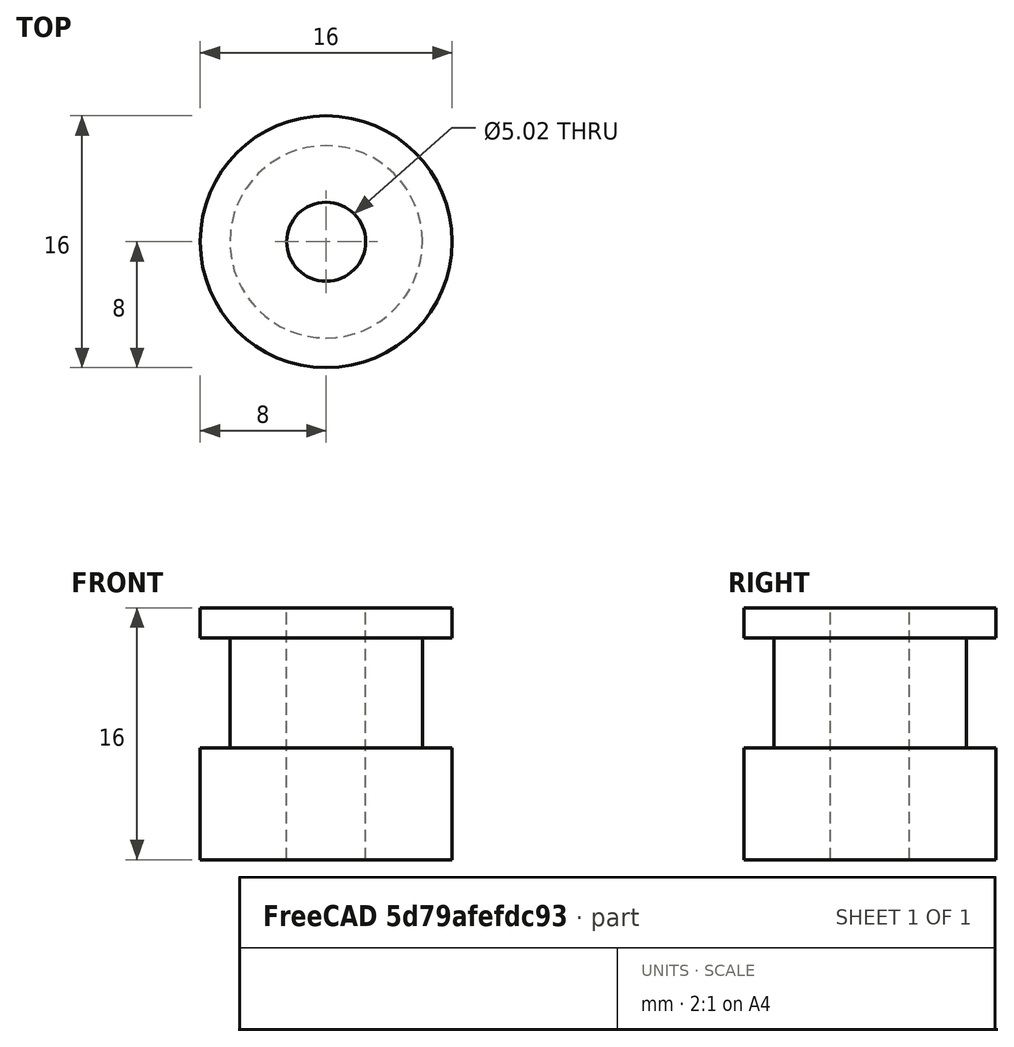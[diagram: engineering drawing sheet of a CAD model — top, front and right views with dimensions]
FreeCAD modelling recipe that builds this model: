
FCSTD DOCUMENT  (FreeCAD 0.20R29177 +426 (Git))
Label: TimingPulleyGT2
License: All rights reserved
LicenseURL: http://en.wikipedia.org/wiki/All_rights_reserved
objects: App::DocumentObjectGroup×3, PartDesign::CoordinateSystem×1, App::FeaturePython×1, Sketcher::SketchObject×1, PartDesign::Revolution×1, PartDesign::Body×1, App::Part×1
note: 5 computed .brp shape members not serialized (recipe doc carries the construction recipe); baked Part::Feature solids carry a one-line shape summary decoded from their .brp

FEATURE [App::DocumentObjectGroup] Parts
FEATURE [PartDesign::CoordinateSystem] LCS_Origin
  AttacherType = Attacher::AttachEngine3D
  MapMode = 2
  Support = -> [X_Axis]
FEATURE [App::FeaturePython] Variables  # WARN: FeaturePython — macro-defined, semantics opaque (R4)
  Type = App::PropertyContainer
FEATURE [App::DocumentObjectGroup] Constraints
FEATURE [App::DocumentObjectGroup] Configurations
FEATURE [Sketcher::SketchObject] Sketch
  FullyConstrained = true
  MapMode = 5
  Placement = pos=(0,0,0) rot=(1,0,0;1.5708rad)
  Support = -> [XZ_Plane001]
  sketch-geometry (8):
    g0: LineSegment StartX=2.51 StartY=0 StartZ=0 EndX=2.51 EndY=16 EndZ=0
    g1: LineSegment StartX=2.51 StartY=16 StartZ=0 EndX=8 EndY=16 EndZ=0
    g2: LineSegment StartX=8 StartY=16 StartZ=0 EndX=8 EndY=14.1 EndZ=0
    g3: LineSegment StartX=8 StartY=14.1 StartZ=0 EndX=6.11 EndY=14.1 EndZ=0
    g4: LineSegment StartX=6.11 StartY=14.1 StartZ=0 EndX=6.11 EndY=7.1 EndZ=0
    g5: LineSegment StartX=6.11 StartY=7.1 StartZ=0 EndX=8 EndY=7.1 EndZ=0
    g6: LineSegment StartX=8 StartY=7.1 StartZ=0 EndX=8 EndY=0 EndZ=0
    g7: LineSegment StartX=8 StartY=0 StartZ=0 EndX=2.51 EndY=0 EndZ=0
  constraints (24):
    c: PointOnObject(g0,g-1)
    c: Vertical(g0)
    c: Coincident(g0,g1)
    c: Horizontal(g1)
    c: Coincident(g1,g2)
    c: Coincident(g2,g3)
    c: Horizontal(g3)
    c: Coincident(g3,g4)
    c: Vertical(g4)
    c: Coincident(g4,g5)
    c: Horizontal(g5)
    c: Coincident(g5,g6)
    c: PointOnObject(g6,g-1)
    c: Vertical(g6)
    c: Coincident(g6,g7)
    c: Coincident(g7,g0)
    c: Vertical(g2)
    c: DistanceX(g-1,g3) = 6.11
    c: DistanceX(g-1,g0) = 2.51
    c: DistanceY(g4,g4) = 7
    c: PointOnObject(g2,g6)
    c: DistanceY(g6,g6) = 7.1
    c: DistanceX(g-1,g6) = 8
    c: DistanceY(g-1,g0) = 16
FEATURE [PartDesign::Revolution] Revolution
  Angle = 360
  Axis = (0,2e-16,1)
  Base = (0,0,0)
  Placement = pos=(0,0,0) rot=(1,0,0;1.5708rad)
  Profile = -> Sketch
  ReferenceAxis = -> Sketch [V_Axis]
  Reversed = true
FEATURE [PartDesign::Body] Body
  Group = -> [Sketch,Revolution]
  Origin = -> Origin001
  Tip = -> Revolution
FEATURE [App::Part] Assembly
  AssemblyType = Part::Link
  Group = -> [LCS_Origin,Variables,Constraints,Configurations,Body]
  Origin = -> Origin
  Type = Assembly
